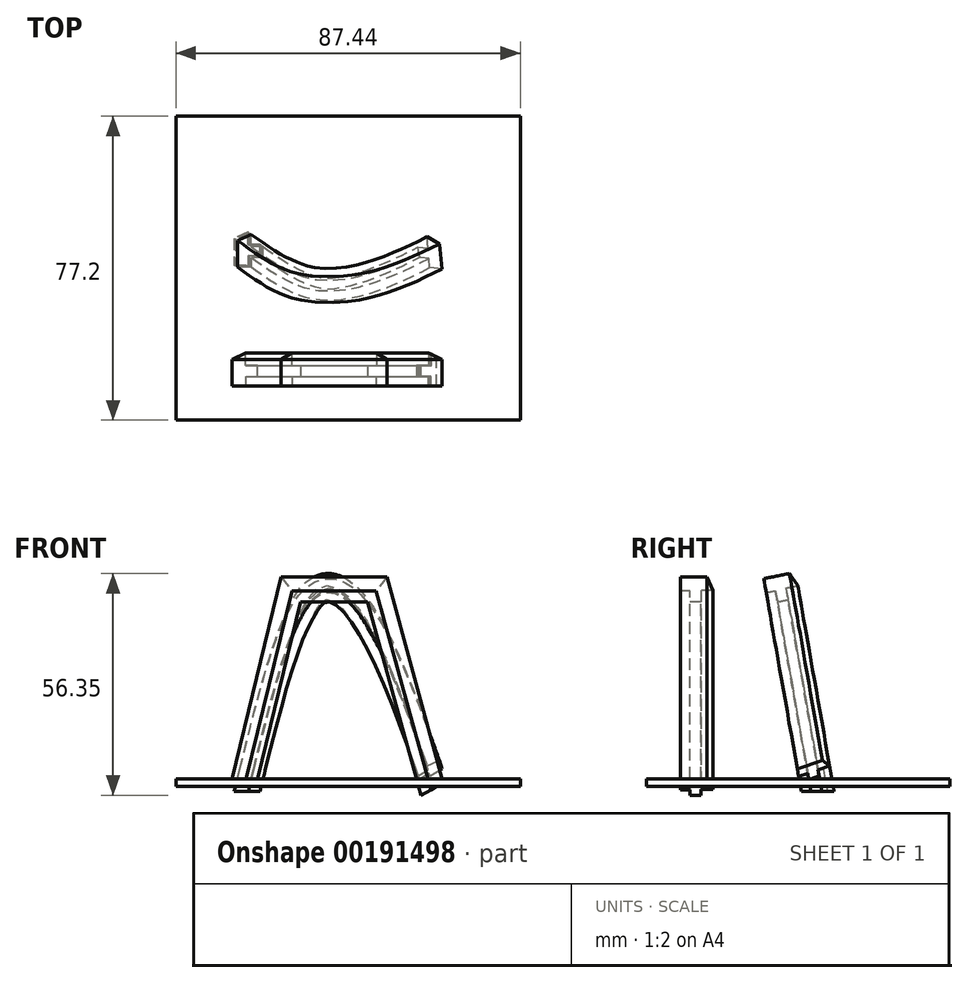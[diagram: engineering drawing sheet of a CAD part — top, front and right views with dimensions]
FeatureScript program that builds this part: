
annotation { "Feature Type Name" : "Feature", "Feature Type Description" : "" }
export const myFeature = defineFeature(function(context is Context, id is Id, definition is map)
    precondition{}
    {
        {
            var Q0;
            Q0=qCreatedBy(makeId("Top.planeOp"),FACE);
            var sketch = newSketch(context, id + "F0", { "sketchPlane" : qUnion([Q0])});
            skLineSegment(sketch, "E0.bottom", {"start": v(-47.3, 39.9) * mm, "end": v(40.15, 39.9) * mm});
            skLineSegment(sketch, "E0.top", {"start": v(-47.3, -37.3) * mm, "end": v(40.15, -37.3) * mm});
            skLineSegment(sketch, "E0.left", {"start": v(-47.3, 39.9) * mm, "end": v(-47.3, -37.3) * mm});
            skLineSegment(sketch, "E0.right", {"start": v(40.15, 39.9) * mm, "end": v(40.15, -37.3) * mm});
            skSolve(sketch);
        }
        {
            var Q0;
            Q0 = qSketchRegion(id + "F0", true);
            extrude(context, id + "F1", {"entities" : qUnion([Q0]), "depth" : 2 * mm});
        }
        {
            var Q0;
            Q0=qCreatedBy(makeId("Front.planeOp"),FACE);
            cPlane(context, id + "F2", {"entities" : qUnion([Q0]), "cplaneType" : CPlaneType.OFFSET, "offset" : 25 * mm, "width" : 150 * mm, "height" : 150 * mm});
        }
        {
            var Q0;
            Q0=qCreatedBy(id+"F2.planeOp",FACE);
            var sketch = newSketch(context, id + "F3", { "sketchPlane" : qUnion([Q0])});
            skLineSegment(sketch, "E1", {"start": v(-31.66, 0) * mm, "end": v(-19.1, 51.35) * mm});
            skLineSegment(sketch, "E2", {"start": v(-19.1, 51.35) * mm, "end": v(4.79, 51.35) * mm});
            skLineSegment(sketch, "E3", {"start": v(4.79, 51.35) * mm, "end": v(18.9, 0) * mm});
            skSolve(sketch);
        }
        {
            var Q0;
            Q0=qCreatedBy(makeId("Top.planeOp"),FACE);
            var sketch = newSketch(context, id + "F4", { "sketchPlane" : qUnion([Q0])});
            skLineSegment(sketch, "E4", {"start": v(-33.62, -21.9) * mm, "end": v(-33.62, -28.67) * mm});
            skLineSegment(sketch, "E5", {"start": v(-33.62, -28.67) * mm, "end": v(-30, -28.67) * mm});
            skLineSegment(sketch, "E6", {"start": v(-30, -28.67) * mm, "end": v(-30, -26.24) * mm});
            skLineSegment(sketch, "E7", {"start": v(-30, -26.24) * mm, "end": v(-27.09, -26.24) * mm});
            skLineSegment(sketch, "E8", {"start": v(-27.09, -26.24) * mm, "end": v(-27.09, -23.44) * mm});
            skLineSegment(sketch, "E9", {"start": v(-27.09, -23.44) * mm, "end": v(-30.13, -23.44) * mm});
            skLineSegment(sketch, "E10", {"start": v(-30.13, -23.44) * mm, "end": v(-30.13, -20.33) * mm});
            skLineSegment(sketch, "E11", {"start": v(-30.13, -20.33) * mm, "end": v(-33.62, -21.9) * mm});
            skLineSegment(sketch, "E12", {"start": v(-32.2, 8.64) * mm, "end": v(-32.2, 1.87) * mm});
            skLineSegment(sketch, "E13", {"start": v(-32.2, 1.87) * mm, "end": v(-28.58, 1.87) * mm});
            skLineSegment(sketch, "E14", {"start": v(-28.58, 1.87) * mm, "end": v(-28.58, 4.3) * mm});
            skLineSegment(sketch, "E15", {"start": v(-28.58, 4.3) * mm, "end": v(-25.67, 4.3) * mm});
            skLineSegment(sketch, "E16", {"start": v(-25.67, 4.3) * mm, "end": v(-25.67, 7.1) * mm});
            skLineSegment(sketch, "E17", {"start": v(-25.67, 7.1) * mm, "end": v(-28.7, 7.1) * mm});
            skLineSegment(sketch, "E18", {"start": v(-28.7, 7.1) * mm, "end": v(-28.7, 10.2) * mm});
            skLineSegment(sketch, "E19", {"start": v(-28.7, 10.2) * mm, "end": v(-32.2, 8.64) * mm});
            skSolve(sketch);
        }
        {
            var Q0;
            Q0=makeQuery(id+"F4.imprint","IMPRINT",FACE,{"disambiguationData":[TD([[makeQuery(id+"F4.imprint","IMPRINT",EDGE,{"derivedFrom":sQuery(id+"F4.wireOp",EDGE,"E4")}),1.0]])]});
            var Q1;
            Q1=sQuery(id+"F3.wireOp",EDGE,"E1");
            var Q2;
            Q2=sQuery(id+"F3.wireOp",EDGE,"E2");
            var Q3;
            Q3=sQuery(id+"F3.wireOp",EDGE,"E3");
            sweep(context, id + "F5", {"operationType" : NewBodyOperationType.ADD, "profiles" : qUnion([Q0]), "path" : qUnion([Q1, Q2, Q3])});
        }
        {
            var Q0;
            Q0=makeQuery(id+"F1.opExtrude","CAP_FACE",FACE,{"disambiguationData":[OSD([sQuery(id+"F0.wireOp",EDGE,"E0.bottom"),sQuery(id+"F0.wireOp",EDGE,"E0.top"),sQuery(id+"F0.wireOp",EDGE,"E0.left"),sQuery(id+"F0.wireOp",EDGE,"E0.right")])],"isStart":false});
            var sketch = newSketch(context, id + "F6", { "sketchPlane" : qUnion([Q0])});
            skLineSegment(sketch, "E20", {"start": v(-24.35, -7.59) * mm, "end": v(18.9, -7.59) * mm});
            skSolve(sketch);
        }
        {
            var Q0;
            Q0=sQuery(id+"F6.wireOp",EDGE,"E20");
            cPlane(context, id + "F7", {"entities" : qUnion([Q0]), "cplaneType" : CPlaneType.LINE_ANGLE, "offset" : 25 * mm, "angle" : 10 * degree, "width" : 150 * mm, "height" : 150 * mm});
        }
        {
            var Q0;
            Q0=qCreatedBy(id+"F7.planeOp",FACE);
            var sketch = newSketch(context, id + "F8", { "sketchPlane" : qUnion([Q0])});
            skFitSpline(sketch, "E21", {"points": [v(-16.5, 0) * mm, v(8.49, 48.04) * mm, v(27.12, 0) * mm], "startDerivative": vector(48, 143.72) * mm, "endDerivative": vector(35.54, -144.54) * mm});
            skSolve(sketch);
        }
        {
            var Q0;
            Q0=makeQuery(id+"F4.imprint","IMPRINT",FACE,{"disambiguationData":[TD([[makeQuery(id+"F4.imprint","IMPRINT",EDGE,{"derivedFrom":sQuery(id+"F4.wireOp",EDGE,"E12")}),1.0]])]});
            var Q1;
            Q1=sQuery(id+"F4.wireOp",EDGE,"E12");
            var Q2;
            Q2=sQuery(id+"F4.wireOp",EDGE,"E13");
            var Q3;
            Q3=sQuery(id+"F4.wireOp",EDGE,"E14");
            var Q4;
            Q4=sQuery(id+"F4.wireOp",EDGE,"E15");
            var Q5;
            Q5=sQuery(id+"F4.wireOp",EDGE,"E16");
            var Q6;
            Q6=sQuery(id+"F4.wireOp",EDGE,"E17");
            var Q7;
            Q7=sQuery(id+"F4.wireOp",EDGE,"E18");
            var Q8;
            Q8=sQuery(id+"F4.wireOp",EDGE,"E19");
            var Q9;
            Q9=sQuery(id+"F8.wireOp",EDGE,"E21");
            sweep(context, id + "F9", {"operationType" : NewBodyOperationType.ADD, "profiles" : qUnion([Q0]), "surfaceProfiles" : qUnion([Q1, Q2, Q3, Q4, Q5, Q6, Q7, Q8]), "path" : qUnion([Q9])});
        }
    });
